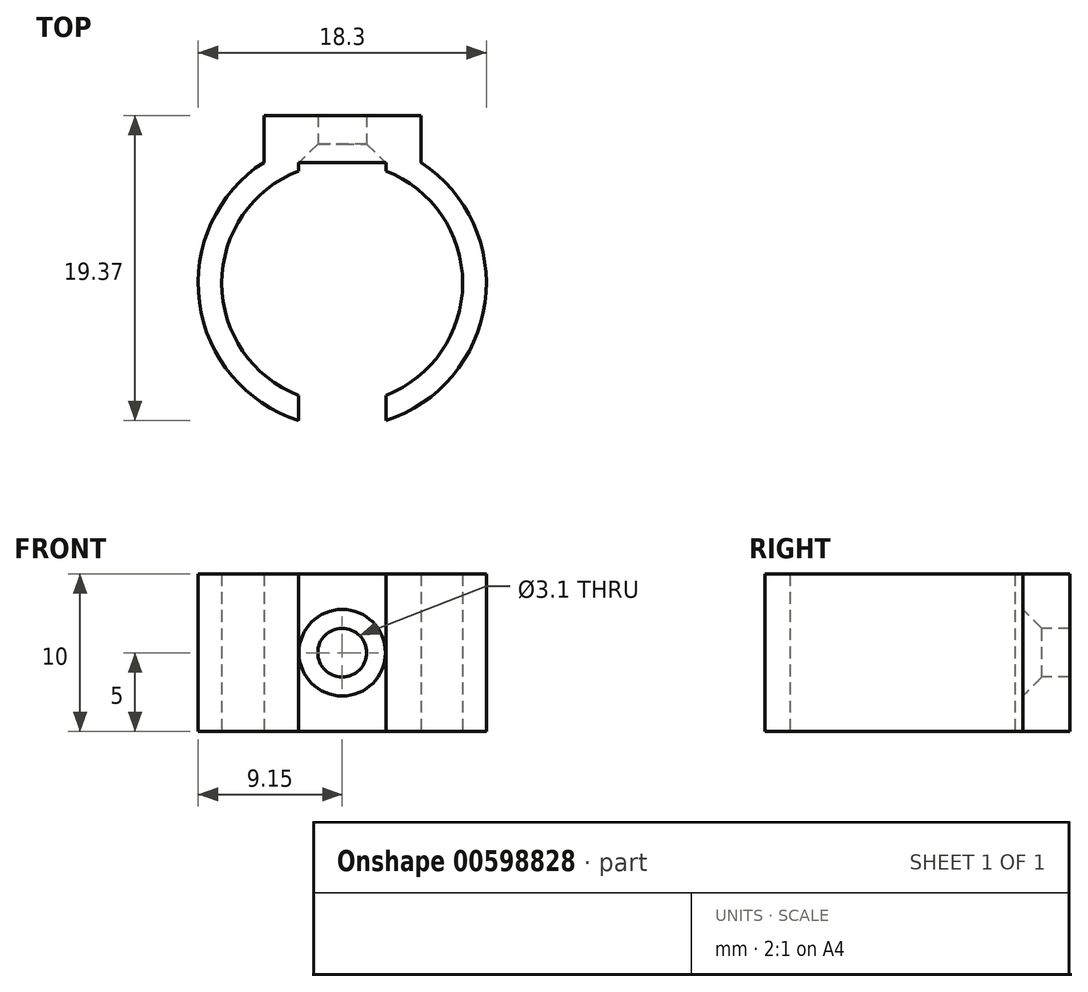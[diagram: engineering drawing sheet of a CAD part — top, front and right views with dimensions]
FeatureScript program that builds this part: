
annotation { "Feature Type Name" : "Feature", "Feature Type Description" : "" }
export const myFeature = defineFeature(function(context is Context, id is Id, definition is map)
    precondition{}
    {
        {
            var Q0;
            Q0=qCreatedBy(makeId("Top.planeOp"),FACE);
            var sketch = newSketch(context, id + "F0", { "sketchPlane" : qUnion([Q0])});
            skLineSegment(sketch, "E0.bottom", {"start": v(5.02, 3) * mm, "end": v(-4.98, 3) * mm});
            skLineSegment(sketch, "E0.top", {"start": v(5.02, 0) * mm, "end": v(-4.98, 0) * mm});
            skLineSegment(sketch, "E0.left", {"start": v(5.02, 3) * mm, "end": v(5.02, 0) * mm});
            skLineSegment(sketch, "E0.right", {"start": v(-4.98, 3) * mm, "end": v(-4.98, 0) * mm});
            skPoint(sketch, "E0.middle", {"position": v(-4.98, 15.28) * mm});
            skCircle(sketch, "E1", {"center": v(0, -7.65) * mm, "radius": 9.15 * mm});
            skCircle(sketch, "E2", {"center": v(0, -7.65) * mm, "radius": 7.65 * mm});
            skLineSegment(sketch, "E3", {"start": v(0, 0) * mm, "end": v(0, -7.65) * mm, "construction": true});
            skSolve(sketch);
        }
        {
            var Q0;
            Q0 = qSketchRegion(id + "F0", true);
            extrude(context, id + "F1", {"entities" : qUnion([Q0]), "depth" : 5 * mm, "offsetDistance" : 25 * mm, "hasSecondDirection" : true, "secondDirectionOppositeDirection" : true, "secondDirectionDepth" : 5 * mm});
        }
        {
            var Q0;
            Q0=qCreatedBy(makeId("Front.planeOp"),FACE);
            var sketch = newSketch(context, id + "F2", { "sketchPlane" : qUnion([Q0])});
            skLineSegment(sketch, "E4.bottom", {"start": v(2.78, -5) * mm, "end": v(-2.77, -5) * mm});
            skLineSegment(sketch, "E4.top", {"start": v(2.77, 5) * mm, "end": v(-2.78, 5) * mm});
            skLineSegment(sketch, "E4.left", {"start": v(2.78, -5) * mm, "end": v(2.77, 5) * mm});
            skLineSegment(sketch, "E4.right", {"start": v(-2.77, -5) * mm, "end": v(-2.78, 5) * mm});
            skPoint(sketch, "E4.middle", {"position": v(0, 0) * mm});
            skSolve(sketch);
        }
        {
            var Q0;
            Q0 = qSketchRegion(id + "F2", true);
            extrude(context, id + "F3", {"entities" : qUnion([Q0]), "operationType" : NewBodyOperationType.REMOVE, "depth" : 25 * mm, "offsetDistance" : 25 * mm});
        }
        {
            var Q0;
            Q0=makeQuery(id+"F3.boolean.opBoolean","COPY",FACE,{"derivedFrom":makeQuery(id+"F3.opExtrude","CAP_FACE",FACE,{"disambiguationData":[OSD([sQuery(id+"F2.wireOp",EDGE,"E4.bottom"),sQuery(id+"F2.wireOp",EDGE,"E4.top"),sQuery(id+"F2.wireOp",EDGE,"E4.left"),sQuery(id+"F2.wireOp",EDGE,"E4.right")])],"isStart":true})});
            var sketch = newSketch(context, id + "F4", { "sketchPlane" : qUnion([Q0])});
            skLineSegment(sketch, "E5", {"start": v(0, 0) * mm, "end": v(0, -5) * mm});
            skSolve(sketch);
        }
        {
            var Q0;
            Q0=sQuery(id+"F4.wireOp",VERTEX,"E5.start");
            var Q1;
            Q1=makeQuery(id+"F1.opExtrude","SWEPT_BODY",BODY,{"disambiguationData":[OSD([sQuery(id+"F0.wireOp",EDGE,"E0.bottom"),sQuery(id+"F0.wireOp",EDGE,"E0.left"),sQuery(id+"F0.wireOp",EDGE,"E0.right"),sQuery(id+"F0.wireOp",EDGE,"E1"),sQuery(id+"F0.wireOp",EDGE,"E2")])]});
            hole(context, id + "F5", {"style" : HoleStyle.C_SINK, "endStyle" : HoleEndStyle.THROUGH, "holeDiameter" : 3.1 * mm, "cSinkDiameter" : 5.5 * mm, "cSinkAngle" : 90 * degree, "majorDiameter" : 3 * mm, "isTappedThrough" : true, "tappedDepth" : 12 * mm, "tapClearance" : 3, "locations" : qUnion([Q0]), "scope" : qUnion([Q1])});
        }
    });
